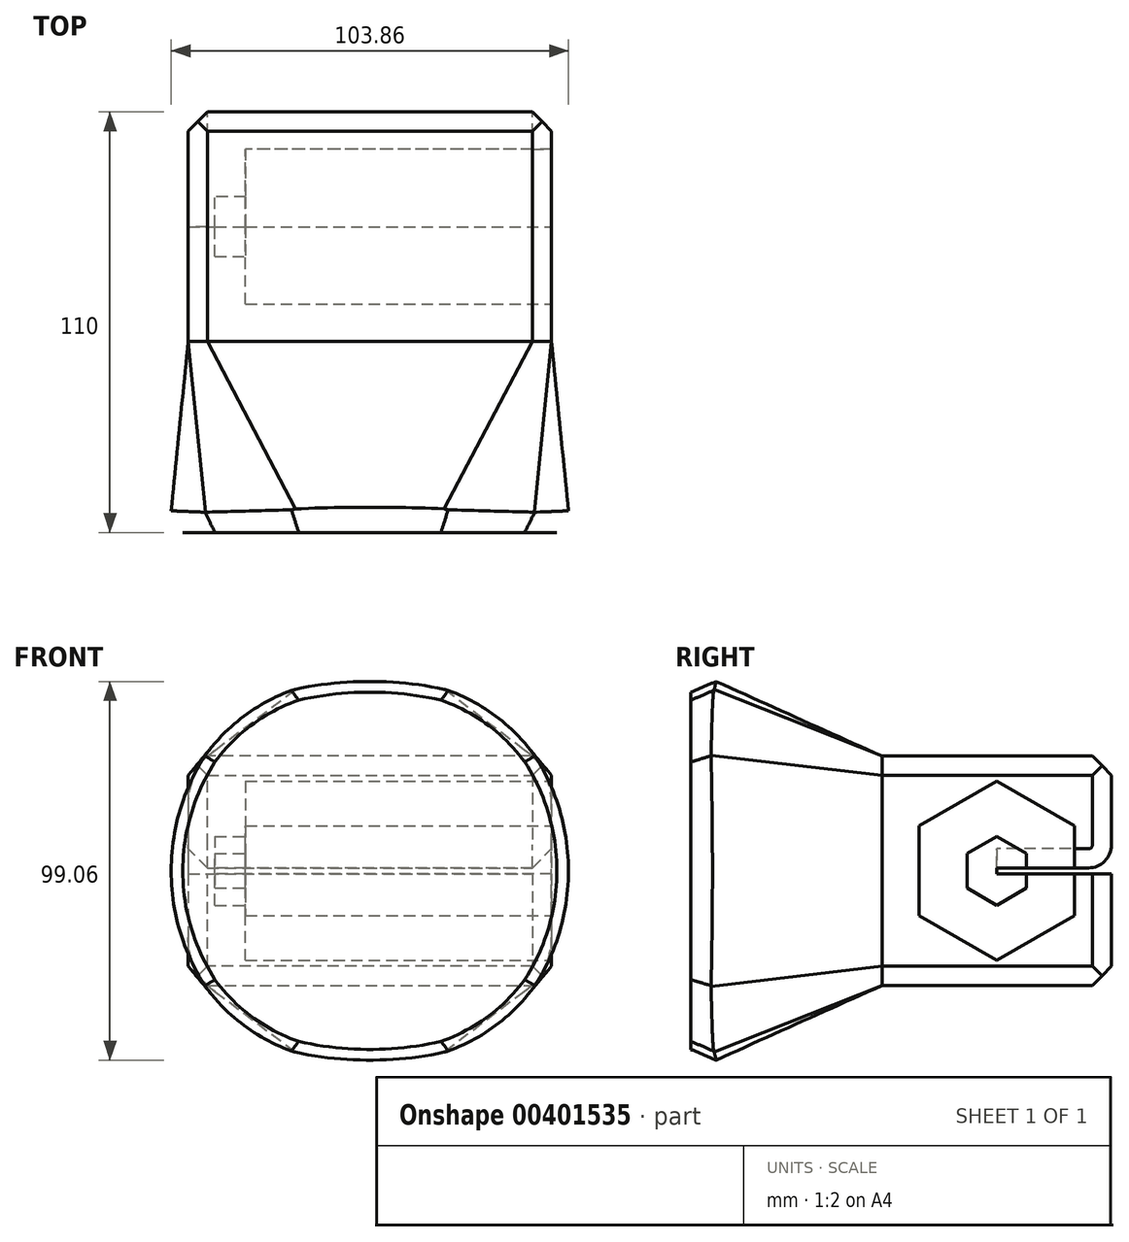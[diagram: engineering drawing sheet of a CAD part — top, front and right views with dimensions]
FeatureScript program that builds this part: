
annotation { "Feature Type Name" : "Feature", "Feature Type Description" : "" }
export const myFeature = defineFeature(function(context is Context, id is Id, definition is map)
    precondition{}
    {
        {
            var Q0;
            Q0=qCreatedBy(makeId("Front.planeOp"),FACE);
            var sketch = newSketch(context, id + "F0", { "sketchPlane" : qUnion([Q0])});
            skLineSegment(sketch, "E0", {"start": v(0, -89.74) * mm, "end": v(0, 103.32) * mm, "construction": true});
            skLineSegment(sketch, "E1", {"start": v(-83.26, 0) * mm, "end": v(88.28, 0) * mm, "construction": true});
            skLineSegment(sketch, "E2.bottom", {"start": v(-47.5, 30) * mm, "end": v(47.5, 30) * mm});
            skLineSegment(sketch, "E2.top", {"start": v(-47.5, -30) * mm, "end": v(47.5, -30) * mm});
            skLineSegment(sketch, "E2.left", {"start": v(-47.5, 30) * mm, "end": v(-47.5, -30) * mm});
            skLineSegment(sketch, "E2.right", {"start": v(47.5, 30) * mm, "end": v(47.5, -30) * mm});
            skSolve(sketch);
        }
        {
            var Q0;
            Q0=makeQuery(id+"F0.imprint","IMPRINT",FACE,{"disambiguationData":[TD([[makeQuery(id+"F0.imprint","IMPRINT",EDGE,{"derivedFrom":sQuery(id+"F0.wireOp",EDGE,"E2.bottom")}),-1.0]])]});
            extrude(context, id + "F1", {"entities" : qUnion([Q0]), "endBound" : BoundingType.SYMMETRIC, "depth" : 60 * mm});
        }
        {
            var Q0;
            Q0=makeQuery(id+"F1.opExtrude","SWEPT_FACE",FACE,{"disambiguationData":[OSD([sQuery(id+"F0.wireOp",EDGE,"E2.right")])]});
            var sketch = newSketch(context, id + "F2", { "sketchPlane" : qUnion([Q0])});
            skCircle(sketch, "E3.cCircle", {"center": v(0, 0) * mm, "radius": 20.3 * mm, "construction": true});
            skLineSegment(sketch, "E3.0", {"start": v(20.3, 11.72) * mm, "end": v(20.3, -11.72) * mm});
            skLineSegment(sketch, "E3.1", {"start": v(20.3, -11.72) * mm, "end": v(0, -23.44) * mm});
            skLineSegment(sketch, "E3.2", {"start": v(0, -23.44) * mm, "end": v(-20.3, -11.72) * mm});
            skLineSegment(sketch, "E3.3", {"start": v(-20.3, -11.72) * mm, "end": v(-20.3, 11.72) * mm});
            skLineSegment(sketch, "E3.4", {"start": v(-20.3, 11.72) * mm, "end": v(0, 23.44) * mm});
            skLineSegment(sketch, "E3.5", {"start": v(0, 23.44) * mm, "end": v(20.3, 11.72) * mm});
            skPoint(sketch, "E3.0.midPoint", {"position": v(20.3, 0) * mm});
            skSolve(sketch);
        }
        {
            var Q0;
            Q0=makeQuery(id+"F2.imprint","IMPRINT",FACE,{"disambiguationData":[TD([[makeQuery(id+"F2.imprint","IMPRINT",EDGE,{"derivedFrom":sQuery(id+"F2.wireOp",EDGE,"E3.0")}),-1.0]])]});
            extrude(context, id + "F3", {"entities" : qUnion([Q0]), "operationType" : NewBodyOperationType.REMOVE, "oppositeDirection" : true, "depth" : 80 * mm});
        }
        {
            var Q0;
            Q0=makeQuery(id+"F3.boolean.opBoolean","COPY",FACE,{"derivedFrom":makeQuery(id+"F3.opExtrude","CAP_FACE",FACE,{"disambiguationData":[OSD([sQuery(id+"F2.wireOp",EDGE,"E3.0"),sQuery(id+"F2.wireOp",EDGE,"E3.1"),sQuery(id+"F2.wireOp",EDGE,"E3.2"),sQuery(id+"F2.wireOp",EDGE,"E3.3"),sQuery(id+"F2.wireOp",EDGE,"E3.4"),sQuery(id+"F2.wireOp",EDGE,"E3.5")])],"isStart":false})});
            var sketch = newSketch(context, id + "F4", { "sketchPlane" : qUnion([Q0])});
            skCircle(sketch, "E4.cCircle", {"center": v(0, 0) * mm, "radius": 7.8 * mm, "construction": true});
            skLineSegment(sketch, "E4.0", {"start": v(7.8, 4.5) * mm, "end": v(7.8, -4.5) * mm});
            skLineSegment(sketch, "E4.1", {"start": v(7.8, -4.5) * mm, "end": v(0, -9) * mm});
            skLineSegment(sketch, "E4.2", {"start": v(0, -9) * mm, "end": v(-7.8, -4.5) * mm});
            skLineSegment(sketch, "E4.3", {"start": v(-7.8, -4.5) * mm, "end": v(-7.8, 4.5) * mm});
            skLineSegment(sketch, "E4.4", {"start": v(-7.8, 4.5) * mm, "end": v(0, 9) * mm});
            skLineSegment(sketch, "E4.5", {"start": v(0, 9) * mm, "end": v(7.8, 4.5) * mm});
            skPoint(sketch, "E4.0.midPoint", {"position": v(7.8, 0) * mm});
            skSolve(sketch);
        }
        {
            var Q0;
            Q0=makeQuery(id+"F4.imprint","IMPRINT",FACE,{"disambiguationData":[TD([[makeQuery(id+"F4.imprint","IMPRINT",EDGE,{"derivedFrom":sQuery(id+"F4.wireOp",EDGE,"E4.0")}),-1.0]])]});
            extrude(context, id + "F5", {"entities" : qUnion([Q0]), "operationType" : NewBodyOperationType.REMOVE, "oppositeDirection" : true, "depth" : 8 * mm});
        }
        {
            var Q0;
            Q0=makeQuery(id+"F1.opExtrude","CAP_FACE",FACE,{"disambiguationData":[OSD([sQuery(id+"F0.wireOp",EDGE,"E2.bottom"),sQuery(id+"F0.wireOp",EDGE,"E2.top"),sQuery(id+"F0.wireOp",EDGE,"E2.left"),sQuery(id+"F0.wireOp",EDGE,"E2.right")])],"isStart":true});
            var sketch = newSketch(context, id + "F6", { "sketchPlane" : qUnion([Q0])});
            skLineSegment(sketch, "E5", {"start": v(55.18, 0) * mm, "end": v(-62.23, 0) * mm, "construction": true});
            skLineSegment(sketch, "E6", {"start": v(0, 44.74) * mm, "end": v(0, -48.92) * mm, "construction": true});
            skPoint(sketch, "E6.endSnap0", {"position": v(0, 30) * mm});
            skLineSegment(sketch, "E7.0", {"start": v(47.5, 30) * mm, "end": v(47.5, -30) * mm, "construction": true});
            skLineSegment(sketch, "E8.0", {"start": v(-47.5, 30) * mm, "end": v(-47.5, -30) * mm, "construction": true});
            skLineSegment(sketch, "E9.bottom", {"start": v(47.5, 0.75) * mm, "end": v(-47.5, 0.75) * mm});
            skLineSegment(sketch, "E9.top", {"start": v(47.5, -0.75) * mm, "end": v(-47.5, -0.75) * mm});
            skLineSegment(sketch, "E9.left", {"start": v(47.5, 0.75) * mm, "end": v(47.5, -0.75) * mm});
            skLineSegment(sketch, "E9.right", {"start": v(-47.5, 0.75) * mm, "end": v(-47.5, -0.75) * mm});
            skSolve(sketch);
        }
        {
            var Q0;
            Q0=makeQuery(id+"F6.imprint","IMPRINT",FACE,{"disambiguationData":[TD([[makeQuery(id+"F6.imprint","IMPRINT",EDGE,{"derivedFrom":sQuery(id+"F6.wireOp",EDGE,"E9.bottom")}),1.0]])]});
            extrude(context, id + "F7", {"entities" : qUnion([Q0]), "operationType" : NewBodyOperationType.REMOVE, "oppositeDirection" : true, "depth" : 30 * mm});
        }
        {
            var Q0;
            Q0=makeQuery(id+"F1.opExtrude","CAP_FACE",FACE,{"disambiguationData":[OSD([sQuery(id+"F0.wireOp",EDGE,"E2.bottom"),sQuery(id+"F0.wireOp",EDGE,"E2.top"),sQuery(id+"F0.wireOp",EDGE,"E2.left"),sQuery(id+"F0.wireOp",EDGE,"E2.right")])],"isStart":false});
            cPlane(context, id + "F8", {"entities" : qUnion([Q0]), "cplaneType" : CPlaneType.OFFSET, "offset" : 50 * mm, "width" : 150 * mm, "height" : 150 * mm});
        }
        {
            var Q0;
            Q0=qCreatedBy(id+"F8.planeOp",FACE);
            var sketch = newSketch(context, id + "F9", { "sketchPlane" : qUnion([Q0])});
            skCircle(sketch, "E10", {"center": v(0, 0) * mm, "radius": 52.5 * mm});
            skSolve(sketch);
        }
        {
            var Q0;
            Q0=qCreatedBy(makeId("Top.planeOp"),FACE);
            var sketch = newSketch(context, id + "F10", { "sketchPlane" : qUnion([Q0])});
            skLineSegment(sketch, "E11.0", {"start": v(-47.5, -30) * mm, "end": v(-47.5, 30) * mm, "construction": true});
            skLineSegment(sketch, "E12.0", {"start": v(52.5, -80) * mm, "end": v(-52.5, -80) * mm, "construction": true});
            skLineSegment(sketch, "E13", {"start": v(-52.5, -80) * mm, "end": v(-47.5, -30) * mm});
            skLineSegment(sketch, "E14.0", {"start": v(47.5, -30) * mm, "end": v(47.5, 30) * mm, "construction": true});
            skLineSegment(sketch, "E15", {"start": v(52.5, -80) * mm, "end": v(47.5, -30) * mm});
            skSolve(sketch);
        }
        {
            var Q0;
            Q0=makeQuery(id+"F1.opExtrude","SWEPT_EDGE",EDGE,{"disambiguationData":[OSD([sQuery(id+"F0.wireOp",EDGE,"E2.bottom"),sQuery(id+"F0.wireOp",EDGE,"E2.right")])]});
            var Q1;
            Q1=makeQuery(id+"F1.opExtrude","SWEPT_EDGE",EDGE,{"disambiguationData":[OSD([sQuery(id+"F0.wireOp",EDGE,"E2.top"),sQuery(id+"F0.wireOp",EDGE,"E2.right")])]});
            var Q2;
            Q2=makeQuery(id+"F1.opExtrude","SWEPT_EDGE",EDGE,{"disambiguationData":[OSD([sQuery(id+"F0.wireOp",EDGE,"E2.top"),sQuery(id+"F0.wireOp",EDGE,"E2.left")])]});
            var Q3;
            Q3=makeQuery(id+"F1.opExtrude","SWEPT_EDGE",EDGE,{"disambiguationData":[OSD([sQuery(id+"F0.wireOp",EDGE,"E2.bottom"),sQuery(id+"F0.wireOp",EDGE,"E2.left")])]});
            chamfer(context, id + "F11", {"entities" : qUnion([Q0, Q1, Q2, Q3]), "width" : 5 * mm, "tangentPropagation" : true});
        }
        {
            var Q1;
            Q1=makeQuery(id+"F1.opExtrude","CAP_FACE",FACE,{"disambiguationData":[OSD([sQuery(id+"F0.wireOp",EDGE,"E2.bottom"),sQuery(id+"F0.wireOp",EDGE,"E2.top"),sQuery(id+"F0.wireOp",EDGE,"E2.left"),sQuery(id+"F0.wireOp",EDGE,"E2.right")])],"isStart":false});
            var Q2;
            Q2=makeQuery(id+"F9.imprint","IMPRINT",FACE,{"disambiguationData":[TD([[makeQuery(id+"F9.imprint","IMPRINT",EDGE,{"derivedFrom":sQuery(id+"F9.wireOp",EDGE,"E10")}),1.0]])]});
            var Q3;
            Q3=sQuery(id+"F10.wireOp",EDGE,"E15");
            var Q4;
            Q4=sQuery(id+"F10.wireOp",EDGE,"E13");
            loft(context, id + "F12", {"operationType" : NewBodyOperationType.ADD, "addGuides" : true, "sheetProfilesArray" : [{ "sheetProfileEntities" : qUnion([Q1]) }, { "sheetProfileEntities" : qUnion([Q2]) }], "guidesArray" : [{ "guideEntities" : qUnion([Q3]), "guideDerivativeType" : LoftGuideDerivativeType.DEFAULT, "guideDerivativeMagnitude" : 1 }, { "guideEntities" : qUnion([Q4]), "guideDerivativeType" : LoftGuideDerivativeType.DEFAULT, "guideDerivativeMagnitude" : 1 }]});
        }
        {
            var Q0;
            Q0=makeQuery(id+"F7.boolean.opBoolean","COPY",EDGE,{"derivedFrom":makeQuery(id+"F7.opExtrude","CAP_EDGE",EDGE,{"disambiguationData":[OSD([sQuery(id+"F6.wireOp",EDGE,"E9.bottom")])],"isStart":true})});
            var Q1;
            Q1=makeQuery(id+"F7.boolean.opBoolean","COPY",EDGE,{"derivedFrom":makeQuery(id+"F7.opExtrude","CAP_EDGE",EDGE,{"disambiguationData":[OSD([sQuery(id+"F6.wireOp",EDGE,"E9.top")])],"isStart":true})});
            fillet(context, id + "F13", {"entities" : qUnion([Q0, Q1]), "radius" : 6 * mm, "tangentPropagation" : true, "allowEdgeOverflow" : false});
        }
        {
            var Q0;
            Q0=makeQuery(id+"F1.opExtrude","CAP_EDGE",EDGE,{"disambiguationData":[OSD([sQuery(id+"F0.wireOp",EDGE,"E2.top")])],"isStart":true});
            var Q1;
            Q1=makeQuery(id+"F1.opExtrude","CAP_EDGE",EDGE,{"disambiguationData":[OSD([sQuery(id+"F0.wireOp",EDGE,"E2.bottom")])],"isStart":true});
            chamfer(context, id + "F14", {"entities" : qUnion([Q0, Q1]), "width" : 5 * mm, "tangentPropagation" : true});
        }
        {
            var Q0;
            Q0=makeQuery(id+"F12.opLoft","MID_CAP_EDGE",EDGE,{"disambiguationData":[OSD([sQuery(id+"F9.wireOp",EDGE,"E10"),sQuery(id+"F10.wireOp",EDGE,"E15")])],"capPos":1.0});
            var Q1;
            Q1=makeQuery(id+"F12.opLoft","MID_CAP_EDGE",EDGE,{"disambiguationData":[OSD([sQuery(id+"F0.wireOp",EDGE,"E2.top"),sQuery(id+"F0.wireOp",EDGE,"E2.left"),sQuery(id+"F9.wireOp",EDGE,"E10"),sQuery(id+"F10.wireOp",EDGE,"E13")])],"capPos":1.0});
            var Q2;
            Q2=makeQuery(id+"F12.opLoft","MID_CAP_EDGE",EDGE,{"disambiguationData":[OSD([sQuery(id+"F9.wireOp",EDGE,"E10"),sQuery(id+"F10.wireOp",EDGE,"E13")])],"capPos":1.0});
            var Q3;
            Q3=makeQuery(id+"F12.opLoft","MID_CAP_EDGE",EDGE,{"disambiguationData":[OSD([sQuery(id+"F0.wireOp",EDGE,"E2.bottom"),sQuery(id+"F0.wireOp",EDGE,"E2.right"),sQuery(id+"F9.wireOp",EDGE,"E10"),sQuery(id+"F10.wireOp",EDGE,"E15")])],"capPos":1.0});
            var Q4;
            {var subQ0=sQuery(id+"F0.wireOp",EDGE,"E2.right");var subQ1=sQuery(id+"F0.wireOp",EDGE,"E2.left");var subQ2=sQuery(id+"F0.wireOp",EDGE,"E2.top");var subQ3=sQuery(id+"F0.wireOp",EDGE,"E2.bottom");var subQ4=makeQuery(id+"F1.opExtrude","CAP_FACE",FACE,{"disambiguationData":[OSD([subQ3,subQ2,subQ1,subQ0])],"isStart":false});var subQ5=makeQuery(id+"F1.opExtrude","SWEPT_EDGE",EDGE,{"disambiguationData":[OSD([subQ3,subQ0])]});var subQ6=sQuery(id+"F9.wireOp",EDGE,"E10");Q4=makeQuery(id+"F12.opLoft","MID_CAP_EDGE",EDGE,{"disambiguationData":[OSD([subQ3,subQ2,subQ1,subQ0,subQ6]),TDD([makeQuery(id+"F9.imprint","IMPRINT",EDGE,{"derivedFrom":subQ6}),makeQuery(id+"F11.opChamfer","BLEND_VERTEX",VERTEX,{"blendedFrom":[subQ5,makeQuery(id+"F1.opExtrude","SWEPT_FACE",FACE,{"disambiguationData":[OSD([subQ3])]}),subQ4],"blendedInto":[makeQuery(id+"F1.opExtrude","SWEPT_FACE",FACE,{"disambiguationData":[OSD([subQ3])]}),subQ4]}),makeQuery(id+"F11.opChamfer","BLEND_VERTEX",VERTEX,{"blendedFrom":[subQ5,subQ4,makeQuery(id+"F1.opExtrude","SWEPT_FACE",FACE,{"disambiguationData":[OSD([subQ0])]})],"blendedInto":[subQ4,makeQuery(id+"F1.opExtrude","SWEPT_FACE",FACE,{"disambiguationData":[OSD([subQ0])]})]})])],"capPos":1.0});}
            var Q5;
            {var subQ0=sQuery(id+"F0.wireOp",EDGE,"E2.right");var subQ1=sQuery(id+"F0.wireOp",EDGE,"E2.left");var subQ2=sQuery(id+"F0.wireOp",EDGE,"E2.top");var subQ3=sQuery(id+"F0.wireOp",EDGE,"E2.bottom");var subQ4=makeQuery(id+"F1.opExtrude","CAP_FACE",FACE,{"disambiguationData":[OSD([subQ3,subQ2,subQ1,subQ0])],"isStart":false});var subQ5=makeQuery(id+"F1.opExtrude","SWEPT_FACE",FACE,{"disambiguationData":[OSD([subQ3])]});var subQ6=sQuery(id+"F9.wireOp",EDGE,"E10");Q5=makeQuery(id+"F12.opLoft","MID_CAP_EDGE",EDGE,{"disambiguationData":[OSD([subQ3,subQ2,subQ1,subQ0,subQ6]),TDD([makeQuery(id+"F9.imprint","IMPRINT",EDGE,{"derivedFrom":subQ6}),makeQuery(id+"F11.opChamfer","BLEND_VERTEX",VERTEX,{"blendedFrom":[makeQuery(id+"F1.opExtrude","SWEPT_EDGE",EDGE,{"disambiguationData":[OSD([subQ3,subQ1])]}),subQ5,subQ4],"blendedInto":[subQ5,subQ4]}),makeQuery(id+"F11.opChamfer","BLEND_VERTEX",VERTEX,{"blendedFrom":[makeQuery(id+"F1.opExtrude","SWEPT_EDGE",EDGE,{"disambiguationData":[OSD([subQ3,subQ0])]}),subQ5,subQ4],"blendedInto":[subQ5,subQ4]})])],"capPos":1.0});}
            var Q6;
            {var subQ0=sQuery(id+"F0.wireOp",EDGE,"E2.left");var subQ1=sQuery(id+"F0.wireOp",EDGE,"E2.right");var subQ2=sQuery(id+"F0.wireOp",EDGE,"E2.top");var subQ3=sQuery(id+"F0.wireOp",EDGE,"E2.bottom");var subQ4=makeQuery(id+"F1.opExtrude","CAP_FACE",FACE,{"disambiguationData":[OSD([subQ3,subQ2,subQ0,subQ1])],"isStart":false});var subQ5=makeQuery(id+"F1.opExtrude","SWEPT_EDGE",EDGE,{"disambiguationData":[OSD([subQ2,subQ0])]});var subQ6=sQuery(id+"F9.wireOp",EDGE,"E10");Q6=makeQuery(id+"F12.opLoft","MID_CAP_EDGE",EDGE,{"disambiguationData":[OSD([subQ3,subQ2,subQ0,subQ1,subQ6]),TDD([makeQuery(id+"F9.imprint","IMPRINT",EDGE,{"derivedFrom":subQ6}),makeQuery(id+"F11.opChamfer","BLEND_VERTEX",VERTEX,{"blendedFrom":[subQ5,subQ4,makeQuery(id+"F1.opExtrude","SWEPT_FACE",FACE,{"disambiguationData":[OSD([subQ2])]})],"blendedInto":[subQ4,makeQuery(id+"F1.opExtrude","SWEPT_FACE",FACE,{"disambiguationData":[OSD([subQ2])]})]}),makeQuery(id+"F11.opChamfer","BLEND_VERTEX",VERTEX,{"blendedFrom":[subQ5,subQ4,makeQuery(id+"F1.opExtrude","SWEPT_FACE",FACE,{"disambiguationData":[OSD([subQ0])]})],"blendedInto":[subQ4,makeQuery(id+"F1.opExtrude","SWEPT_FACE",FACE,{"disambiguationData":[OSD([subQ0])]})]})])],"capPos":1.0});}
            var Q7;
            {var subQ0=sQuery(id+"F0.wireOp",EDGE,"E2.top");var subQ1=makeQuery(id+"F1.opExtrude","SWEPT_FACE",FACE,{"disambiguationData":[OSD([subQ0])]});var subQ2=sQuery(id+"F0.wireOp",EDGE,"E2.right");var subQ3=sQuery(id+"F0.wireOp",EDGE,"E2.left");var subQ4=sQuery(id+"F0.wireOp",EDGE,"E2.bottom");var subQ5=makeQuery(id+"F1.opExtrude","CAP_FACE",FACE,{"disambiguationData":[OSD([subQ4,subQ0,subQ3,subQ2])],"isStart":false});var subQ6=sQuery(id+"F9.wireOp",EDGE,"E10");Q7=makeQuery(id+"F12.opLoft","MID_CAP_EDGE",EDGE,{"disambiguationData":[OSD([subQ4,subQ0,subQ3,subQ2,subQ6]),TDD([makeQuery(id+"F9.imprint","IMPRINT",EDGE,{"derivedFrom":subQ6}),makeQuery(id+"F11.opChamfer","BLEND_VERTEX",VERTEX,{"blendedFrom":[makeQuery(id+"F1.opExtrude","SWEPT_EDGE",EDGE,{"disambiguationData":[OSD([subQ0,subQ3])]}),subQ5,subQ1],"blendedInto":[subQ5,subQ1]}),makeQuery(id+"F11.opChamfer","BLEND_VERTEX",VERTEX,{"blendedFrom":[makeQuery(id+"F1.opExtrude","SWEPT_EDGE",EDGE,{"disambiguationData":[OSD([subQ0,subQ2])]}),subQ5,subQ1],"blendedInto":[subQ5,subQ1]})])],"capPos":1.0});}
            chamfer(context, id + "F15", {"entities" : qUnion([Q0, Q1, Q2, Q3, Q4, Q5, Q6, Q7]), "chamferType" : ChamferType.OFFSET_ANGLE, "width" : 3 * mm, "oppositeDirection" : false, "angle" : 60 * degree, "tangentPropagation" : true});
        }
        {
            var Q0;
            {var subQ0=sQuery(id+"F0.wireOp",EDGE,"E2.bottom");var subQ1=sQuery(id+"F0.wireOp",EDGE,"E2.left");Q0=makeQuery(id+"F7.boolean.opBoolean","SPLIT",EDGE,{"disambiguationData":[TD([makeQuery(id+"F1.opExtrude","SWEPT_FACE",FACE,{"disambiguationData":[OSD([subQ0])]})])],"derivedFrom":makeQuery(id+"F1.opExtrude","CAP_EDGE",EDGE,{"disambiguationData":[OSD([subQ1])],"isStart":true})});}
            var Q1;
            {var subQ0=sQuery(id+"F0.wireOp",EDGE,"E2.left");var subQ1=sQuery(id+"F0.wireOp",EDGE,"E2.top");Q1=makeQuery(id+"F7.boolean.opBoolean","SPLIT",EDGE,{"disambiguationData":[TD([makeQuery(id+"F1.opExtrude","SWEPT_FACE",FACE,{"disambiguationData":[OSD([subQ1])]})])],"derivedFrom":makeQuery(id+"F1.opExtrude","CAP_EDGE",EDGE,{"disambiguationData":[OSD([subQ0])],"isStart":true})});}
            var Q2;
            {var subQ0=sQuery(id+"F0.wireOp",EDGE,"E2.bottom");var subQ1=sQuery(id+"F0.wireOp",EDGE,"E2.right");Q2=makeQuery(id+"F7.boolean.opBoolean","SPLIT",EDGE,{"disambiguationData":[TD([makeQuery(id+"F1.opExtrude","SWEPT_FACE",FACE,{"disambiguationData":[OSD([subQ0])]})])],"derivedFrom":makeQuery(id+"F1.opExtrude","CAP_EDGE",EDGE,{"disambiguationData":[OSD([subQ1])],"isStart":true})});}
            var Q3;
            {var subQ0=sQuery(id+"F0.wireOp",EDGE,"E2.right");var subQ1=sQuery(id+"F0.wireOp",EDGE,"E2.top");Q3=makeQuery(id+"F7.boolean.opBoolean","SPLIT",EDGE,{"disambiguationData":[TD([makeQuery(id+"F1.opExtrude","SWEPT_FACE",FACE,{"disambiguationData":[OSD([subQ1])]})])],"derivedFrom":makeQuery(id+"F1.opExtrude","CAP_EDGE",EDGE,{"disambiguationData":[OSD([subQ0])],"isStart":true})});}
            chamfer(context, id + "F16", {"entities" : qUnion([Q0, Q1, Q2, Q3]), "width" : 5 * mm, "tangentPropagation" : true});
        }
    });
